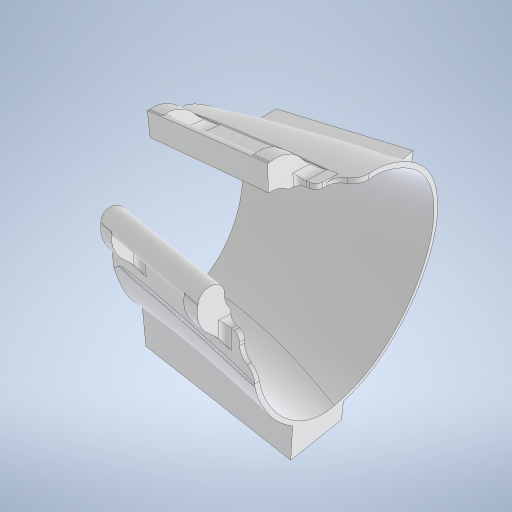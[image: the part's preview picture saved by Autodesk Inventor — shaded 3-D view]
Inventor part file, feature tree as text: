
AUTODESK INVENTOR PART (.ipt)
format: ipt  version: 2023 (Build 270158000, 158)  size: 3,585,536 bytes
history: native  units: in
note: dims shown in document units (in); Inventor stores cm internally (conversion verified against a paired STEP export)
features: delete_face x16, other x15, fillet x11, plane x5, sketch x5, imported_body x3, extrude x2, move_body x2, shell x1
ambient origin geometry x8: Origin, YZ Plane, XZ Plane, XY Plane, X Axis, Y Axis, Z Axis, Center Point
bodies: Volumenkörper12 (feature_tree), Volumenkörper14 (feature_tree), Volumenkörper15 (feature_tree), Volumenkörper16 (feature_tree)
feature tree (60):
  plane  "Arbeitsebene10"
  sketch  "Skizze11"  dims[d110=0.0in d111=90.0deg d112=0.0in d113=90.0deg d114=0.1969in d115=0.0in d116=0.1969in d117=0.0in d118=0.0591in d121=0.3937in d122=0.0in d125=0.1575in d126=0.1575in d127=0.1575in d128=0.1575in d129=0.1575in]
  plane  "Arbeitsebene11"
  sketch  "Skizze12"  dims[d130=0.1575in d131=0.1575in]
  plane  "Arbeitsebene12"
  sketch  "Skizze13"  dims[d132=0.1575in]
  plane  "Arbeitsebene13"
  sketch  "Skizze14"  dims[d133=0.1575in]
  plane  "Arbeitsebene14"
  other  "Fläche heften3"
  shell  "Wandung2"  Thickness=0.0in
  extrude  "Extrusion4"  TaperAngle=0.0deg  [1 undecoded]
  delete_face  "Fläche löschen20"
  other  "3D-Skizze5"
  imported_body  "Basis1"
  other  "Kombinieren2"
  delete_face  "Fläche löschen5"
  imported_body  "Basis2"
  delete_face  "Fläche löschen6"
  delete_face  "Fläche löschen7"
  imported_body  "Basis3"
  other  "Kombinieren5"
  fillet  "Rundung2"  Radius=0.1969in
  fillet  "Rundung3"  [1 undecoded]
  delete_face  "Fläche löschen10"
  delete_face  "Fläche löschen11"
  delete_face  "Fläche löschen12"
  fillet  "Rundung4"  Radius=0.1969in
  delete_face  "Fläche löschen13"
  fillet  "Rundung5"  [1 undecoded]
  fillet  "Rundung6"  Radius=0.0591in
  delete_face  "Fläche löschen14"
  delete_face  "Fläche löschen15"
  fillet  "Rundung7"  Radius=0.3937in
  delete_face  "Fläche löschen16"
  fillet  "Rundung8"  Radius=0.1575in
  delete_face  "Fläche löschen17"
  fillet  "Rundung9"  Radius=0.1575in
  delete_face  "Fläche löschen18"
  fillet  "Rundung10"  Radius=0.1575in
  fillet  "Rundung11"  Radius=0.1575in
  fillet  "Rundung12"  Radius=0.1575in
  delete_face  "Fläche löschen19"
  extrude  "Extrusion5"  Depth=0.1575in
  delete_face  "Fläche löschen21"
  delete_face  "Fläche löschen22"
  move_body  "Move Body18"
  move_body  "Move Body19"
  sketch  "Skizze15"  dims[d134=0.1575in d135=0.0787in d138=0.7874in d139=0.5906in d140=0.3937in d141=0.0in d142=19.685in d143=0.0in d144=0.0in d145=-3.7402in d146=-1.9685in d147=0.0in d49=0.0197in d50=0.0344in d51=0.0197in d52=0.0344in d123=0.0197in d124=0.0344in d136=0.0in d137=0.0in]
  other  "Flä13"
  other  "Form7"
  other  "Flä15"
  other  "Flä16"
  other  "Kurve auf Fläche1"
  other  "Flä17"
  other  "Erhabene Fläche2"
  other  "Entfalten1"
  other  "Flä14"
  other  "Umgrenzungsfläche4"
  other  "Umgrenzungsfläche5"
note: 3 required parameter values undecoded (feature->parameter linkage not recoverable at this tier; creation-order binding heuristic only, values carry confidence <= 0.55)
